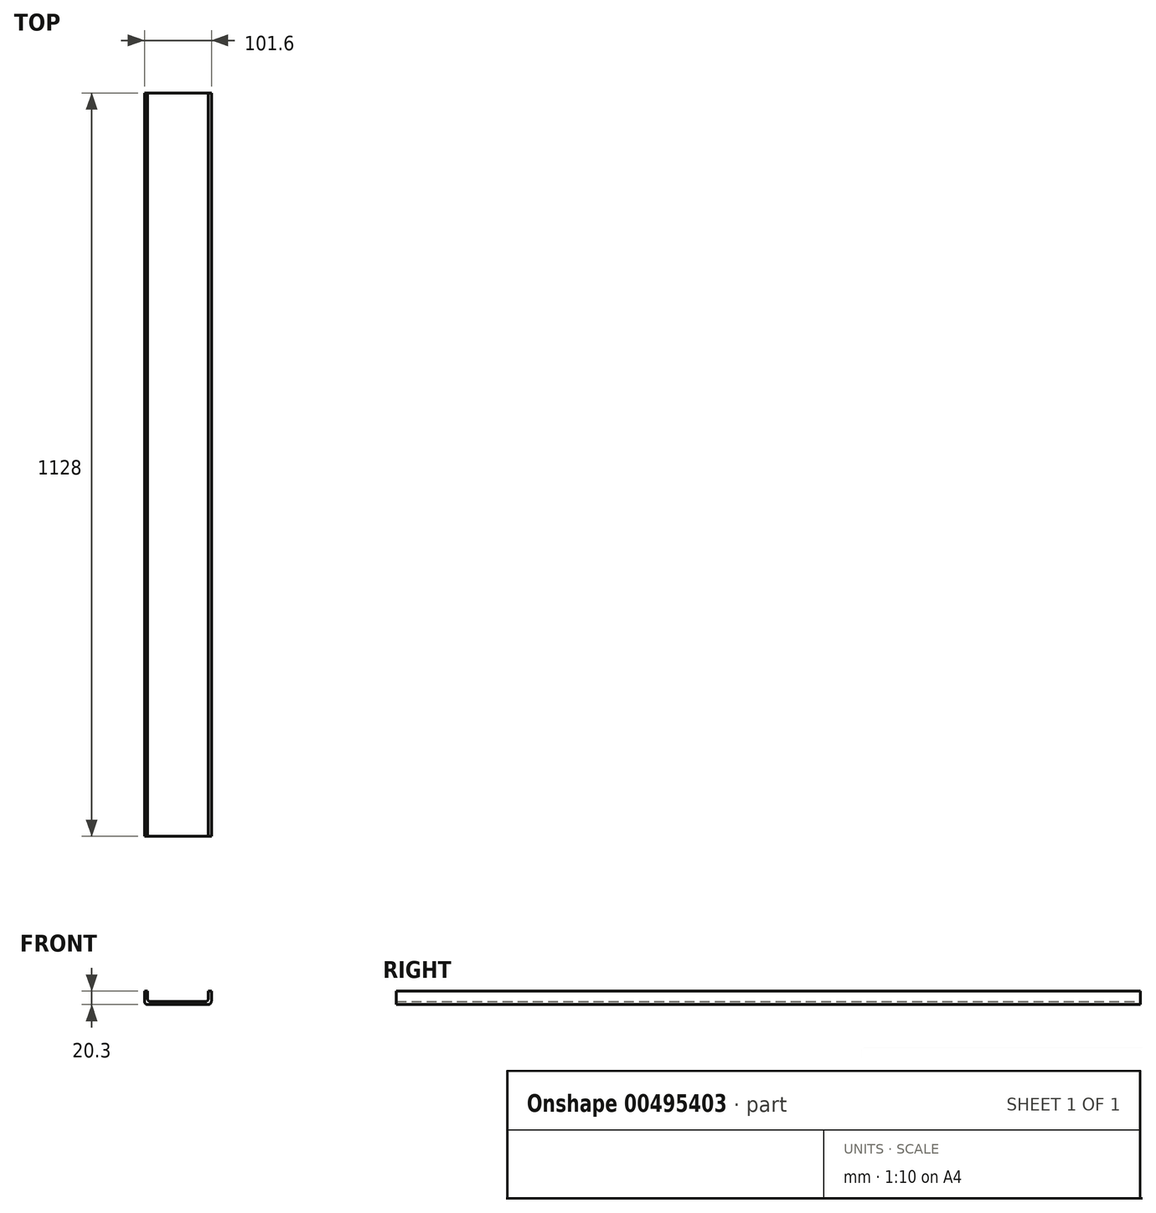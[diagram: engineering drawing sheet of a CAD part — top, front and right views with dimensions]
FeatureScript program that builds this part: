
annotation { "Feature Type Name" : "Feature", "Feature Type Description" : "" }
export const myFeature = defineFeature(function(context is Context, id is Id, definition is map)
    precondition{}
    {
        {
            var Q0;
            Q0=qCreatedBy(makeId("Front.planeOp"),FACE);
            var sketch = newSketch(context, id + "F0", { "sketchPlane" : qUnion([Q0])});
            skLineSegment(sketch, "E0", {"start": v(5, 0) * mm, "end": v(96.6, 0) * mm});
            skLineSegment(sketch, "E1", {"start": v(0, 5) * mm, "end": v(0, 20.3) * mm});
            skLineSegment(sketch, "E2", {"start": v(101.6, 5) * mm, "end": v(101.6, 20.3) * mm});
            skLineSegment(sketch, "E3.0", {"start": v(4.5, 9.5) * mm, "end": v(4.5, 20.3) * mm});
            skLineSegment(sketch, "E3.1", {"start": v(9.5, 4.5) * mm, "end": v(92.1, 4.5) * mm});
            skLineSegment(sketch, "E3.2", {"start": v(97.1, 9.5) * mm, "end": v(97.1, 20.3) * mm});
            skPoint(sketch, "E4.visualSharp", {"position": v(0, 0) * mm});
            skArc(sketch, "E4.filletArc", {"start": v(0, 5) * mm, "mid": v(1.46, 1.46) * mm, "end": v(5, 0) * mm});
            skPoint(sketch, "E5.visualSharp", {"position": v(4.5, 4.5) * mm});
            skArc(sketch, "E5.filletArc", {"start": v(4.5, 9.5) * mm, "mid": v(5.96, 5.96) * mm, "end": v(9.5, 4.5) * mm});
            skPoint(sketch, "E6.visualSharp", {"position": v(97.1, 4.5) * mm});
            skArc(sketch, "E6.filletArc", {"start": v(92.1, 4.5) * mm, "mid": v(95.64, 5.96) * mm, "end": v(97.1, 9.5) * mm});
            skPoint(sketch, "E7.visualSharp", {"position": v(101.6, 0) * mm});
            skArc(sketch, "E7.filletArc", {"start": v(96.6, 0) * mm, "mid": v(100.14, 1.46) * mm, "end": v(101.6, 5) * mm});
            skLineSegment(sketch, "E8", {"start": v(0, 20.3) * mm, "end": v(4.5, 20.3) * mm});
            skLineSegment(sketch, "E9", {"start": v(97.1, 20.3) * mm, "end": v(101.6, 20.3) * mm});
            skSolve(sketch);
        }
        {
            var Q0;
            Q0=makeQuery(id+"F0.imprint","IMPRINT",FACE,{"disambiguationData":[TD([[makeQuery(id+"F0.imprint","IMPRINT",EDGE,{"derivedFrom":sQuery(id+"F0.wireOp",EDGE,"E0")}),1.0]])]});
            extrude(context, id + "F1", {"entities" : qUnion([Q0]), "depth" : 1128 * mm});
        }
    });
